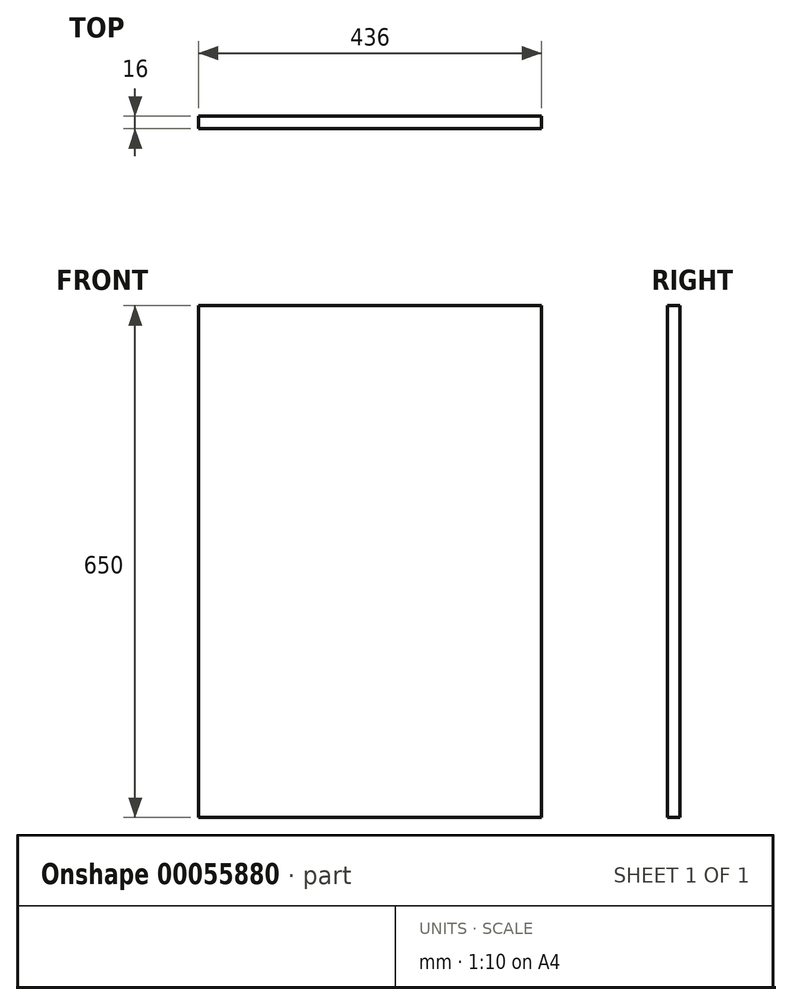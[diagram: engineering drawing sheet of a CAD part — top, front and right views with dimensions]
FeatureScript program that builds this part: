
annotation { "Feature Type Name" : "Feature", "Feature Type Description" : "" }
export const myFeature = defineFeature(function(context is Context, id is Id, definition is map)
    precondition{}
    {
        {
            var Q0;
            Q0=qCreatedBy(makeId("Front.planeOp"),FACE);
            var sketch = newSketch(context, id + "F0", { "sketchPlane" : qUnion([Q0])});
            skLineSegment(sketch, "E0.rect.bottom", {"start": v(-218, 325) * mm, "end": v(218, 325) * mm});
            skLineSegment(sketch, "E0.rect.top", {"start": v(-218, -325) * mm, "end": v(218, -325) * mm});
            skLineSegment(sketch, "E0.rect.left", {"start": v(-218, 325) * mm, "end": v(-218, -325) * mm});
            skLineSegment(sketch, "E0.rect.right", {"start": v(218, 325) * mm, "end": v(218, -325) * mm});
            skPoint(sketch, "E0.rect.middle", {"position": v(0, 0) * mm});
            skSolve(sketch);
        }
        {
            var Q0;
            Q0=makeQuery(id+"F0.imprint","IMPRINT",FACE,{"disambiguationData":[TD([[makeQuery(id+"F0.imprint","IMPRINT",EDGE,{"derivedFrom":sQuery(id+"F0.wireOp",EDGE,"E0.rect.bottom")}),-1.0]])]});
            extrude(context, id + "F1", {"entities" : qUnion([Q0]), "oppositeDirection" : true, "depth" : 16 * mm});
        }
    });
